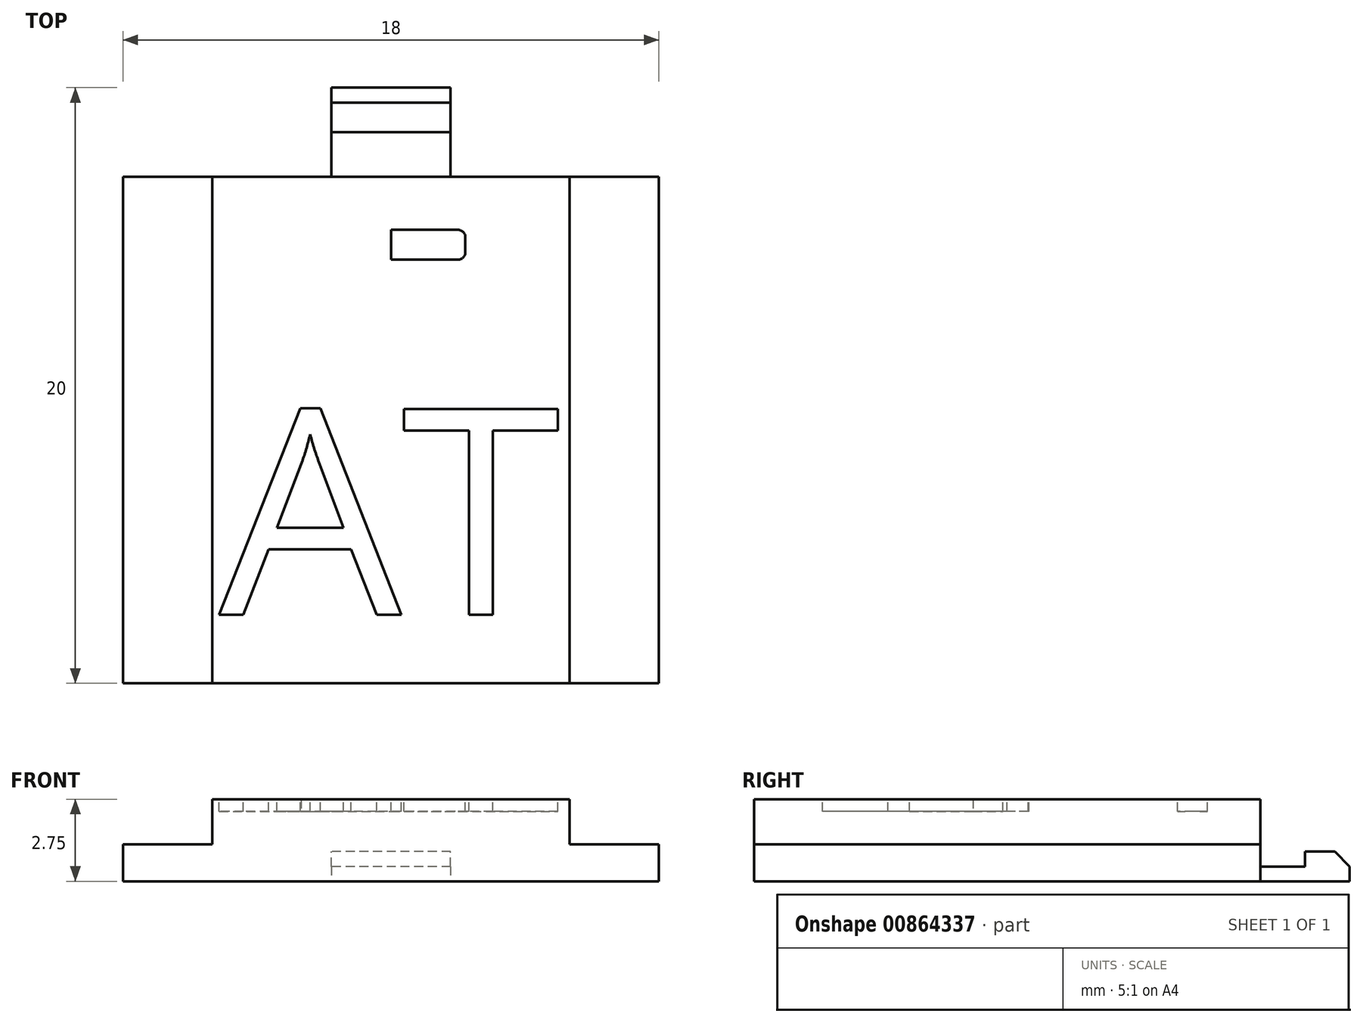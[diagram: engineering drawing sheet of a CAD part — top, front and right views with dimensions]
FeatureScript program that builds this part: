
annotation { "Feature Type Name" : "Feature", "Feature Type Description" : "" }
export const myFeature = defineFeature(function(context is Context, id is Id, definition is map)
    precondition{}
    {
        {
            var Q0;
            Q0=qCreatedBy(makeId("Front.planeOp"),FACE);
            var sketch = newSketch(context, id + "F0", { "sketchPlane" : qUnion([Q0])});
            skLineSegment(sketch, "E0.bottom", {"start": v(9, 0.63) * mm, "end": v(-9, 0.63) * mm});
            skLineSegment(sketch, "E0.top", {"start": v(9, -0.62) * mm, "end": v(-9, -0.62) * mm});
            skLineSegment(sketch, "E0.left", {"start": v(9, 0.63) * mm, "end": v(9, -0.62) * mm});
            skLineSegment(sketch, "E0.right", {"start": v(-9, 0.63) * mm, "end": v(-9, -0.62) * mm});
            skPoint(sketch, "E0.middle", {"position": v(0, 0) * mm});
            skSolve(sketch);
        }
        {
            var Q0;
            Q0=makeQuery(id+"F0.imprint","IMPRINT",FACE,{"disambiguationData":[TD([[makeQuery(id+"F0.imprint","IMPRINT",EDGE,{"derivedFrom":sQuery(id+"F0.wireOp",EDGE,"E0.bottom")}),1.0]])]});
            extrude(context, id + "F1", {"entities" : qUnion([Q0]), "depth" : 17 * mm, "offsetDistance" : 25 * mm});
        }
        {
            var Q0;
            Q0=makeQuery(id+"F1.opExtrude","SWEPT_FACE",FACE,{"disambiguationData":[OSD([sQuery(id+"F0.wireOp",EDGE,"E0.bottom")])]});
            var sketch = newSketch(context, id + "F2", { "sketchPlane" : qUnion([Q0])});
            skLineSegment(sketch, "E1", {"start": v(-9, 0) * mm, "end": v(-6, 0) * mm});
            skLineSegment(sketch, "E2", {"start": v(9, 0) * mm, "end": v(6, 0) * mm});
            skLineSegment(sketch, "E3", {"start": v(-6, 0) * mm, "end": v(-6, -17) * mm});
            skLineSegment(sketch, "E4", {"start": v(6, 0) * mm, "end": v(6, -17) * mm});
            skSolve(sketch);
        }
        {
            var Q0;
            {var subQ0=sQuery(id+"F2.wireOp",EDGE,"E3");Q0=makeQuery(id+"F2.imprint","IMPRINT",FACE,{"disambiguationData":[TD([[makeQuery(id+"F2.imprint","IMPRINT",EDGE,{"derivedFrom":subQ0}),1.0]])]});}
            extrude(context, id + "F3", {"entities" : qUnion([Q0]), "operationType" : NewBodyOperationType.ADD, "depth" : 1.5 * mm, "offsetDistance" : 25 * mm});
        }
        {
            var Q0;
            {var subQ0=sQuery(id+"F0.wireOp",EDGE,"E0.bottom");var subQ1=makeQuery(id+"F1.opExtrude","CAP_EDGE",EDGE,{"disambiguationData":[OSD([subQ0])],"isStart":true});Q0=makeQuery(id+"F3.boolean.opBoolean","MERGE",FACE,{"derivedFrom":[makeQuery(id+"F1.opExtrude","CAP_FACE",FACE,{"disambiguationData":[OSD([subQ0,sQuery(id+"F0.wireOp",EDGE,"E0.top"),sQuery(id+"F0.wireOp",EDGE,"E0.left"),sQuery(id+"F0.wireOp",EDGE,"E0.right")])],"isStart":true}),makeQuery(id+"F3.opExtrude","SWEPT_FACE",FACE,{"disambiguationData":[OSD([subQ0]),TDD([makeQuery(id+"F2.imprint","IMPRINT",EDGE,{"disambiguationData":[TD([[makeQuery(id+"F2.imprint","INTERSECT",VERTEX,{"derivedFrom":[subQ1,sQuery(id+"F2.wireOp",EDGE,"E1"),sQuery(id+"F2.wireOp",EDGE,"E3")]}),1.0]])],"derivedFrom":subQ1})])]})]});}
            var sketch = newSketch(context, id + "F4", { "sketchPlane" : qUnion([Q0])});
            skLineSegment(sketch, "E5", {"start": v(-9, -0.62) * mm, "end": v(0, -0.62) * mm});
            skLineSegment(sketch, "E6", {"start": v(-2, 0.38) * mm, "end": v(-2, -0.62) * mm});
            skLineSegment(sketch, "E7", {"start": v(2, 0.38) * mm, "end": v(2, -0.62) * mm});
            skLineSegment(sketch, "E8", {"start": v(-2, 0.38) * mm, "end": v(2, 0.38) * mm});
            skSolve(sketch);
        }
        {
            var Q0;
            {var subQ1=sQuery(id+"F4.wireOp",EDGE,"E6");Q0=makeQuery(id+"F4.imprint","IMPRINT",FACE,{"disambiguationData":[TD([[makeQuery(id+"F4.imprint","IMPRINT",EDGE,{"derivedFrom":subQ1}),1.0]])]});}
            extrude(context, id + "F5", {"entities" : qUnion([Q0]), "operationType" : NewBodyOperationType.ADD, "depth" : 3 * mm, "offsetDistance" : 25 * mm});
        }
        {
            var Q0;
            Q0=makeQuery(id+"F5.opExtrude","SWEPT_FACE",FACE,{"disambiguationData":[OSD([sQuery(id+"F4.wireOp",EDGE,"E8")])]});
            var sketch = newSketch(context, id + "F6", { "sketchPlane" : qUnion([Q0])});
            skLineSegment(sketch, "E9", {"start": v(-2, 1.5) * mm, "end": v(2, 1.5) * mm});
            skSolve(sketch);
        }
        {
            var Q0;
            {var subQ0=sQuery(id+"F6.wireOp",EDGE,"E9");Q0=makeQuery(id+"F6.imprint","IMPRINT",FACE,{"disambiguationData":[TD([[makeQuery(id+"F6.imprint","IMPRINT",EDGE,{"derivedFrom":subQ0}),-1.0]])]});}
            extrude(context, id + "F7", {"entities" : qUnion([Q0]), "operationType" : NewBodyOperationType.REMOVE, "oppositeDirection" : true, "depth" : .5 * mm, "offsetDistance" : 25 * mm});
        }
        {
            var Q0;
            Q0=makeQuery(id+"F5.opExtrude","SWEPT_FACE",FACE,{"disambiguationData":[OSD([sQuery(id+"F4.wireOp",EDGE,"E7")])]});
            var sketch = newSketch(context, id + "F8", { "sketchPlane" : qUnion([Q0])});
            skLineSegment(sketch, "E10", {"start": v(-1.5, -0.12) * mm, "end": v(-3, -0.12) * mm});
            skLineSegment(sketch, "E11", {"start": v(-1.5, 0.38) * mm, "end": v(-2.5, 0.38) * mm});
            skLineSegment(sketch, "E12", {"start": v(-3, -0.12) * mm, "end": v(-2.5, 0.38) * mm});
            skSolve(sketch);
        }
        {
            var Q0;
            {var subQ0=sQuery(id+"F8.wireOp",EDGE,"E12");Q0=makeQuery(id+"F8.imprint","IMPRINT",FACE,{"disambiguationData":[TD([[makeQuery(id+"F8.imprint","IMPRINT",EDGE,{"derivedFrom":subQ0}),1.0]])]});}
            extrude(context, id + "F9", {"entities" : qUnion([Q0]), "operationType" : NewBodyOperationType.REMOVE, "oppositeDirection" : true, "depth" : 25 * mm, "offsetDistance" : 25 * mm});
        }
        {
            var Q0;
            Q0=makeQuery(id+"F3.opExtrude","CAP_FACE",FACE,{"disambiguationData":[OSD([sQuery(id+"F0.wireOp",EDGE,"E0.bottom"),sQuery(id+"F2.wireOp",EDGE,"E3"),sQuery(id+"F2.wireOp",EDGE,"E4")])],"isStart":false});
            var sketch = newSketch(context, id + "F10", { "sketchPlane" : qUnion([Q0])});
            skLineSegment(sketch, "E13", {"start": v(0, 0) * mm, "end": v(0, -17) * mm});
            skLineSegment(sketch, "E14", {"start": v(0, -1.78) * mm, "end": v(-2.5, -1.78) * mm});
            skLineSegment(sketch, "E15", {"start": v(-2.25, -1.78) * mm, "end": v(0, -1.78) * mm});
            skLineSegment(sketch, "E16", {"start": v(0, -1.78) * mm, "end": v(2.25, -1.78) * mm});
            skLineSegment(sketch, "E17", {"start": v(-2.5, -2.02) * mm, "end": v(-2.5, -2.53) * mm});
            skLineSegment(sketch, "E18", {"start": v(2.5, -2.03) * mm, "end": v(2.5, -2.53) * mm});
            skLineSegment(sketch, "E19", {"start": v(-2.25, -2.78) * mm, "end": v(2.25, -2.78) * mm});
            skPoint(sketch, "E20.visualSharp", {"position": v(-2.5, -1.78) * mm});
            skArc(sketch, "E20.filletArc", {"start": v(-2.25, -1.78) * mm, "mid": v(-2.43, -1.85) * mm, "end": v(-2.5, -2.02) * mm});
            skPoint(sketch, "E21.visualSharp", {"position": v(-2.5, -2.78) * mm});
            skArc(sketch, "E21.filletArc", {"start": v(-2.5, -2.53) * mm, "mid": v(-2.43, -2.7) * mm, "end": v(-2.25, -2.78) * mm});
            skPoint(sketch, "E22.visualSharp", {"position": v(2.5, -2.78) * mm});
            skArc(sketch, "E22.filletArc", {"start": v(2.25, -2.78) * mm, "mid": v(2.43, -2.7) * mm, "end": v(2.5, -2.53) * mm});
            skPoint(sketch, "E23.visualSharp", {"position": v(2.5, -1.78) * mm});
            skArc(sketch, "E23.filletArc", {"start": v(2.5, -2.03) * mm, "mid": v(2.43, -1.85) * mm, "end": v(2.25, -1.78) * mm});
            skText(sketch, "E24", { "text": "AT", "fontName": "OpenSans-Regular.ttf"});
            const initialGuessF10  = {"E24": [-0.00577, -0.0147, 1, 0, 0.00696]};
            skSetInitialGuess(sketch, initialGuessF10);
            skSolve(sketch);
        }
        {
            var Q0;
            {var subQ4=sQuery(id+"F10.wireOp",EDGE,"E15");Q0=makeQuery(id+"F10.imprint","IMPRINT",FACE,{"disambiguationData":[TD([[makeQuery(id+"F10.imprint","IMPRINT",EDGE,{"derivedFrom":subQ4}),-1.0]])]});}
            var Q1;
            {var subQ4=sQuery(id+"F10.wireOp",EDGE,"E16");Q1=makeQuery(id+"F10.imprint","IMPRINT",FACE,{"disambiguationData":[TD([[makeQuery(id+"F10.imprint","IMPRINT",EDGE,{"derivedFrom":subQ4}),-1.0]])]});}
            var Q2;
            {var subQ1=sQuery(id+"F10.wireOp",EDGE,"E24.sketch_text.stroke-0");Q2=makeQuery(id+"F10.imprint","IMPRINT",FACE,{"disambiguationData":[TD([[makeQuery(id+"F10.imprint","IMPRINT",EDGE,{"derivedFrom":subQ1}),-1.0]])]});}
            var Q3;
            Q3=makeQuery(id+"F10.imprint","IMPRINT",FACE,{"disambiguationData":[TD([[makeQuery(id+"F10.imprint","IMPRINT",EDGE,{"derivedFrom":sQuery(id+"F10.wireOp",EDGE,"E24.sketch_text.stroke-13")}),-1.0]])]});
            var Q4;
            {var subQ0=sQuery(id+"F10.wireOp",EDGE,"E24.sketch_text.stroke-6");var subQ1=sQuery(id+"F10.wireOp",EDGE,"E13");var subQ2=makeQuery(id+"F10.imprint","INTERSECT",VERTEX,{"derivedFrom":[subQ1,subQ0]});Q4=makeQuery(id+"F10.imprint","IMPRINT",FACE,{"disambiguationData":[TD([[makeQuery(id+"F10.imprint","IMPRINT",EDGE,{"disambiguationData":[TD([[subQ2,-1.0]])],"derivedFrom":subQ1}),1.0]])]});}
            extrude(context, id + "F11", {"entities" : qUnion([Q0, Q1, Q2, Q3, Q4]), "operationType" : NewBodyOperationType.REMOVE, "oppositeDirection" : true, "depth" : .4 * mm, "offsetDistance" : 25 * mm});
        }
    });
